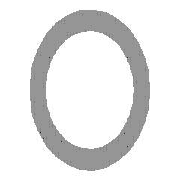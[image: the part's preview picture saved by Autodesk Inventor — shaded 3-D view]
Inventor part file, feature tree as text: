
AUTODESK INVENTOR PART (.ipt)
format: ipt  version: 2021 (Build 250183000, 183)  size: 381,952 bytes
history: native  units: mm (DEFAULTED — no unit token found)
features: other x7, plane x3, sketch x3, sweep x1, split x1
ambient origin geometry x8: Origin, YZ Plane, XZ Plane, XY Plane, X Axis, Y Axis, Z Axis, Center Point
bodies: Solid1 (feature_tree)
feature tree (15):
  parser-record x1  (decoder bookkeeping rows leaked as tree rows — omitted from the tree; the rows remain in map.json)
  other  "Driven Length"
  other  "Plano inicial"
  other  "Plano final"
  other  "Trayectoria de barrido"
  plane  "Plano de trabajo de orientación"
  sweep  "Cuerpo"
  plane  "Plano de trabajo9"
  split  "Dividir5"
  sketch  "Sketch3"  dims[d0=26.67mm d1=3.9116mm]
  plane  "Work Plane3"
  sketch  "Sketch4"  dims[d4=-0.0mm]
  sketch  "Boceto9"  dims[d5=1126.193571mm d6=90.0deg d7=1126.193571mm d8=0.0mm d9=0.0mm d26=0.0mm d27=90.0deg d28=0.0mm d29=90.0deg]
  other  "Sup5"
  other  "SuperficieSolevación5"
